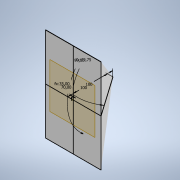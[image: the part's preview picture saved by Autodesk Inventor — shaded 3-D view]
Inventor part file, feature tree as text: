
AUTODESK INVENTOR PART (.ipt)
format: ipt  version: 2022 (Build 260153000, 153)  size: 119,808 bytes
history: native  units: mm
features: sketch x5, other x2, extrude x2, projected_geometry x1
ambient origin geometry x8: Origin, YZ Plane, XZ Plane, XY Plane, X Axis, Y Axis, Z Axis, Center Point
bodies: Body1 (feature_tree)
feature tree (10):
  other  "Твердое тело1"
  sketch  "Эскиз1"
  sketch  "Эскиз2"
  other  "РабПлоскость1"
  sketch  "Эскиз3"
  extrude  "Выдавливание1"  Depth=12.217305mm
  extrude  "Выдавливание2"  Depth=6.108652mm
  sketch  "Эскиз4"
  sketch  "Эскиз5"
  projected_geometry  "Спроецированная петля1"
